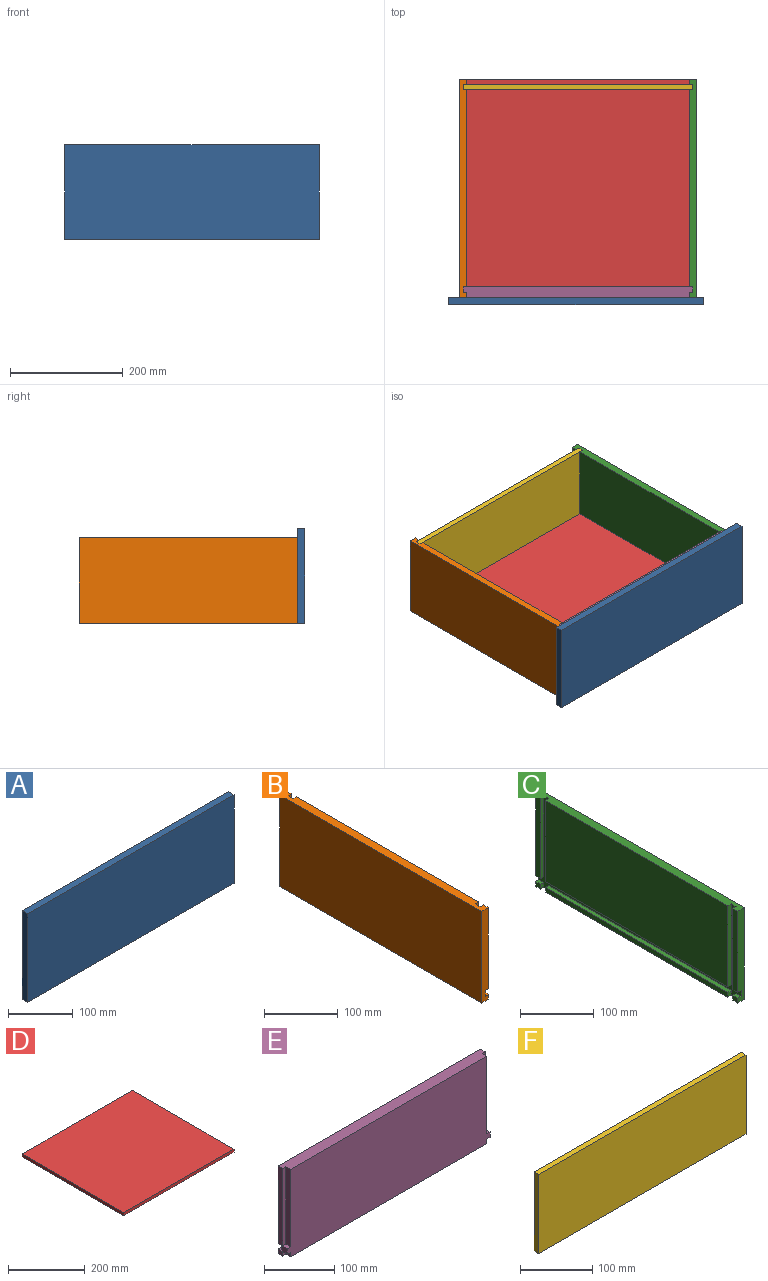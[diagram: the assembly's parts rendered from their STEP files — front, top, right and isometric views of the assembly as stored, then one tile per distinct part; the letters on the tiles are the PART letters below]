
ASSEMBLY  parts=6 mates=5
PART A: 6 faces, bbox 451.6x12.7x167.7 mm
  f0: plane 167.74x12.7mm, normal (1,0,0), area 2130.3mm2, adj f1,f3,f4,f5
  f1: plane 451.64x12.7mm, normal (0,0,1), area 5735.8mm2, adj f0,f2,f4,f5
  f2: plane 167.74x12.7mm, normal (-1,0,0), area 2130.3mm2, adj f1,f3,f4,f5
  f3: plane 451.64x12.7mm, normal (0,0,-1), area 5735.8mm2, adj f0,f2,f4,f5
  f4: plane 451.64x167.74mm, normal (0,-1,0), area 75758.4mm2, adj f0,f1,f2,f3
  f5: plane 451.64x167.74mm, normal (0,1,0), area 75758.4mm2, adj f0,f1,f2,f3
PART B: 26 faces, bbox 12.7x387.4x151.9 mm
  f0: plane 9.53x7.92mm, normal (1,0,0), area 75.5mm2, adj f3,f11,f14,f23
  f1: plane 134.42x9.53mm, normal (1,0,0), area 1280.3mm2, adj f2,f4,f14,f24
  f2: plane 387.35x12.7mm, normal (0,0,1), area 4798.4mm2, adj f1,f6,f9,f12,f13,f14,f17,f18
  f3: plane 9.53x6.35mm, normal (0,0,1), area 60.5mm2, adj f0,f14,f17,f23
  f4: plane 9.53x6.35mm, normal (0,0,-1), area 60.5mm2, adj f1,f14,f17,f24
  f5: plane 349.25x7.92mm, normal (1,0,0), area 2767.7mm2, adj f7,f11,f21,f22
  f6: plane 349.25x134.42mm, normal (1,0,0), area 46945.1mm2, adj f2,f8,f18,f25
  f7: plane 349.25x6.35mm, normal (0,0,1), area 2217.7mm2, adj f5,f17,f21,f22
  f8: plane 349.25x6.35mm, normal (0,0,-1), area 2217.7mm2, adj f6,f17,f18,f25
  f9: plane 151.87x12.7mm, normal (0,1,0), area 1868.2mm2, adj f2,f10,f11,f12,f13,f15,f16,f17
  f10: plane 9.53x7.92mm, normal (1,0,0), area 75.5mm2, adj f9,f11,f15,f20
  f11: plane 387.35x12.7mm, normal (0,0,-1), area 4798.4mm2, adj f0,f5,f9,f10,f12,f14,f17,f20
  f12: plane 387.35x151.87mm, normal (-1,0,0), area 58825.5mm2, adj f2,f9,f11,f14
  f13: plane 134.42x9.53mm, normal (1,0,0), area 1280.3mm2, adj f2,f9,f16,f19
  f14: plane 151.87x12.7mm, normal (0,-1,0), area 1868.2mm2, adj f0,f1,f2,f3,f4,f11,f12,f17
  f15: plane 9.53x6.35mm, normal (0,0,1), area 60.5mm2, adj f9,f10,f17,f20
  f16: plane 9.53x6.35mm, normal (0,0,-1), area 60.5mm2, adj f9,f13,f17,f19
  f17: plane 387.35x151.87mm, normal (1,0,0), area 6401.1mm2, adj f2,f3,f4,f7,f8,f9,f11,f14
  f18: plane 134.42x6.35mm, normal (0,1,0), area 853.5mm2, adj f2,f6,f8,f17
  f19: plane 134.42x6.35mm, normal (0,-1,0), area 853.5mm2, adj f2,f13,f16,f17
  f20: plane 7.92x6.35mm, normal (0,-1,0), area 50.3mm2, adj f10,f11,f15,f17
  f21: plane 7.92x6.35mm, normal (0,1,0), area 50.3mm2, adj f5,f7,f11,f17
  f22: plane 7.92x6.35mm, normal (0,-1,0), area 50.3mm2, adj f5,f7,f11,f17
  f23: plane 7.92x6.35mm, normal (0,1,0), area 50.3mm2, adj f0,f3,f11,f17
  f24: plane 134.42x6.35mm, normal (0,1,0), area 853.5mm2, adj f1,f2,f4,f17
  f25: plane 134.42x6.35mm, normal (0,-1,0), area 853.5mm2, adj f2,f6,f8,f17
PART C: 26 faces, bbox 12.7x387.4x151.9 mm
  f0: plane 9.53x7.92mm, normal (-1,0,0), area 75.5mm2, adj f3,f11,f14,f23
  f1: plane 134.42x9.53mm, normal (-1,0,0), area 1280.3mm2, adj f2,f4,f14,f24
  f2: plane 387.35x12.7mm, normal (0,0,1), area 4798.4mm2, adj f1,f6,f9,f12,f13,f14,f17,f18
  f3: plane 9.53x6.35mm, normal (0,0,1), area 60.5mm2, adj f0,f14,f17,f23
  f4: plane 9.53x6.35mm, normal (0,0,-1), area 60.5mm2, adj f1,f14,f17,f24
  f5: plane 349.25x7.92mm, normal (-1,0,0), area 2767.7mm2, adj f7,f11,f21,f22
  f6: plane 349.25x134.42mm, normal (-1,0,0), area 46945.1mm2, adj f2,f8,f18,f25
  f7: plane 349.25x6.35mm, normal (0,0,1), area 2217.7mm2, adj f5,f17,f21,f22
  f8: plane 349.25x6.35mm, normal (0,0,-1), area 2217.7mm2, adj f6,f17,f18,f25
  f9: plane 151.87x12.7mm, normal (0,1,0), area 1868.2mm2, adj f2,f10,f11,f12,f13,f15,f16,f17
  f10: plane 9.53x7.92mm, normal (-1,0,0), area 75.5mm2, adj f9,f11,f15,f20
  f11: plane 387.35x12.7mm, normal (0,0,-1), area 4798.4mm2, adj f0,f5,f9,f10,f12,f14,f17,f20
  f12: plane 387.35x151.87mm, normal (1,0,0), area 58825.5mm2, adj f2,f9,f11,f14
  f13: plane 134.42x9.53mm, normal (-1,0,0), area 1280.3mm2, adj f2,f9,f16,f19
  f14: plane 151.87x12.7mm, normal (0,-1,0), area 1868.2mm2, adj f0,f1,f2,f3,f4,f11,f12,f17
  f15: plane 9.53x6.35mm, normal (0,0,1), area 60.5mm2, adj f9,f10,f17,f20
  f16: plane 9.53x6.35mm, normal (0,0,-1), area 60.5mm2, adj f9,f13,f17,f19
  f17: plane 387.35x151.87mm, normal (-1,0,0), area 6401.1mm2, adj f2,f3,f4,f7,f8,f9,f11,f14
  f18: plane 134.42x6.35mm, normal (0,1,0), area 853.5mm2, adj f2,f6,f8,f17
  f19: plane 134.42x6.35mm, normal (0,-1,0), area 853.5mm2, adj f2,f13,f16,f17
  f20: plane 7.92x6.35mm, normal (0,-1,0), area 50.3mm2, adj f10,f11,f15,f17
  f21: plane 7.92x6.35mm, normal (0,1,0), area 50.3mm2, adj f5,f7,f11,f17
  f22: plane 7.92x6.35mm, normal (0,-1,0), area 50.3mm2, adj f5,f7,f11,f17
  f23: plane 7.92x6.35mm, normal (0,1,0), area 50.3mm2, adj f0,f3,f11,f17
  f24: plane 134.42x6.35mm, normal (0,1,0), area 853.5mm2, adj f1,f2,f4,f17
  f25: plane 134.42x6.35mm, normal (0,-1,0), area 853.5mm2, adj f2,f6,f8,f17
PART D: 6 faces, bbox 406.4x376.2x9.5 mm
  f0: plane 376.22x9.53mm, normal (1,0,0), area 3583.5mm2, adj f1,f2,f3,f4
  f1: plane 406.4x9.53mm, normal (0,1,0), area 3871mm2, adj f0,f3,f4,f5
  f2: plane 406.4x9.53mm, normal (0,-1,0), area 3871mm2, adj f0,f3,f4,f5
  f3: plane 406.4x376.22mm, normal (0,0,-1), area 152897.8mm2, adj f0,f1,f2,f5
  f4: plane 406.4x376.22mm, normal (0,0,1), area 152897.8mm2, adj f0,f1,f2,f5
  f5: plane 376.22x9.53mm, normal (-1,0,0), area 3583.5mm2, adj f1,f2,f3,f4
PART E: 22 faces, bbox 406.4x19.1x151.9 mm
  f0: plane 9.53x7.92mm, normal (1,0,0), area 75.5mm2, adj f1,f2,f11,f12
  f1: plane 9.53x6.35mm, normal (0,0,-1), area 60.5mm2, adj f0,f2,f3,f11
  f2: plane 7.92x6.35mm, normal (0,-1,0), area 50.3mm2, adj f0,f1,f3,f12
  f3: plane 151.87x19.05mm, normal (1,0,0), area 1461.8mm2, adj f1,f2,f4,f5,f7,f8,f9,f10
  f4: plane 9.53x6.35mm, normal (0,0,1), area 60.5mm2, adj f3,f5,f6,f11
  f5: plane 134.42x6.35mm, normal (0,-1,0), area 853.5mm2, adj f3,f4,f6,f10
  f6: plane 134.42x9.53mm, normal (1,0,0), area 1280.3mm2, adj f4,f5,f10,f11
  f7: plane 406.4x7.92mm, normal (0,0,1), area 3220.6mm2, adj f3,f8,f13,f18
  f8: plane 406.4x9.53mm, normal (0,1,0), area 3871mm2, adj f3,f7,f9,f18
  f9: plane 406.4x7.92mm, normal (0,0,-1), area 3220.6mm2, adj f3,f8,f14,f18
  f10: plane 406.4x19.05mm, normal (0,0,1), area 7621mm2, adj f3,f5,f6,f11,f14,f18,f20,f21
  f11: plane 406.4x151.87mm, normal (0,-1,0), area 59910.8mm2, adj f0,f1,f3,f4,f6,f10,f12,f15
  f12: plane 406.4x19.05mm, normal (0,0,-1), area 7621mm2, adj f0,f2,f3,f11,f13,f15,f17,f18
  f13: plane 406.4x7.92mm, normal (0,1,0), area 3220.6mm2, adj f3,f7,f12,f18
  f14: plane 406.4x134.42mm, normal (0,1,0), area 54627mm2, adj f3,f9,f10,f18
  f15: plane 9.53x7.92mm, normal (-1,0,0), area 75.5mm2, adj f11,f12,f16,f17
  f16: plane 9.53x6.35mm, normal (0,0,-1), area 60.5mm2, adj f11,f15,f17,f18
  f17: plane 7.92x6.35mm, normal (0,-1,0), area 50.3mm2, adj f12,f15,f16,f18
  f18: plane 151.87x19.05mm, normal (-1,0,0), area 1461.8mm2, adj f7,f8,f9,f10,f11,f12,f13,f14
  f19: plane 9.53x6.35mm, normal (0,0,1), area 60.5mm2, adj f11,f18,f20,f21
  f20: plane 134.42x6.35mm, normal (0,-1,0), area 853.5mm2, adj f10,f18,f19,f21
  f21: plane 134.42x9.53mm, normal (-1,0,0), area 1280.3mm2, adj f10,f11,f19,f20
PART F: 6 faces, bbox 406.4x9.5x134.4 mm
  f0: plane 134.42x9.53mm, normal (1,0,0), area 1280.3mm2, adj f1,f2,f3,f4
  f1: plane 406.4x9.53mm, normal (0,0,-1), area 3871mm2, adj f0,f3,f4,f5
  f2: plane 406.4x9.53mm, normal (0,0,1), area 3871mm2, adj f0,f3,f4,f5
  f3: plane 406.4x134.42mm, normal (0,-1,0), area 54627mm2, adj f0,f1,f2,f5
  f4: plane 406.4x134.42mm, normal (0,1,0), area 54627mm2, adj f0,f1,f2,f5
  f5: plane 134.42x9.53mm, normal (-1,0,0), area 1280.3mm2, adj f1,f2,f3,f4
PLACE A t=(-8.74,0,0)mm
PLACE B at identity fixed
PLACE C at identity
PLACE D at identity
PLACE E at identity
PLACE F at identity
MATE fastened C.f11 <-> A.f3  axis (0,0,-1) through (-279.4,-406.4,402.16)mm
MATE fastened F.f2 <-> C.f2  axis (0,0,1) through (-285.75,-38.1,554.02)mm
MATE fastened D.f1 <-> C.f9  axis (0,1,0) through (-285.75,-19.05,419.61)mm
MATE fastened F.f2 <-> B.f2  axis (0,0,1) through (-692.15,-38.1,554.02)mm
MATE fastened C.f2 <-> E.f10  axis (0,0,1) through (-292.1,-406.4,554.02)mm
